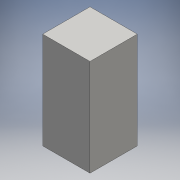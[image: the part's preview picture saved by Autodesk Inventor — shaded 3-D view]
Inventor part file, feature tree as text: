
AUTODESK INVENTOR PART (.ipt)
format: ipt  version: 2016 (Build 200138000, 138)  size: 84,480 bytes
history: native  units: mm
features: other x1, extrude x1, sketch x1
ambient origin geometry x8: Origin, YZ Plane, XZ Plane, XY Plane, X Axis, Y Axis, Z Axis, Center Point
bodies: Body1 (feature_tree)
feature tree (3):
  other  "Sólido1"
  extrude  "Extrusión1"  Depth=45.0mm
  sketch  "Boceto1"  dims[d0=22.0mm d1=45.0mm d2=22.0mm d3=0.0mm]
